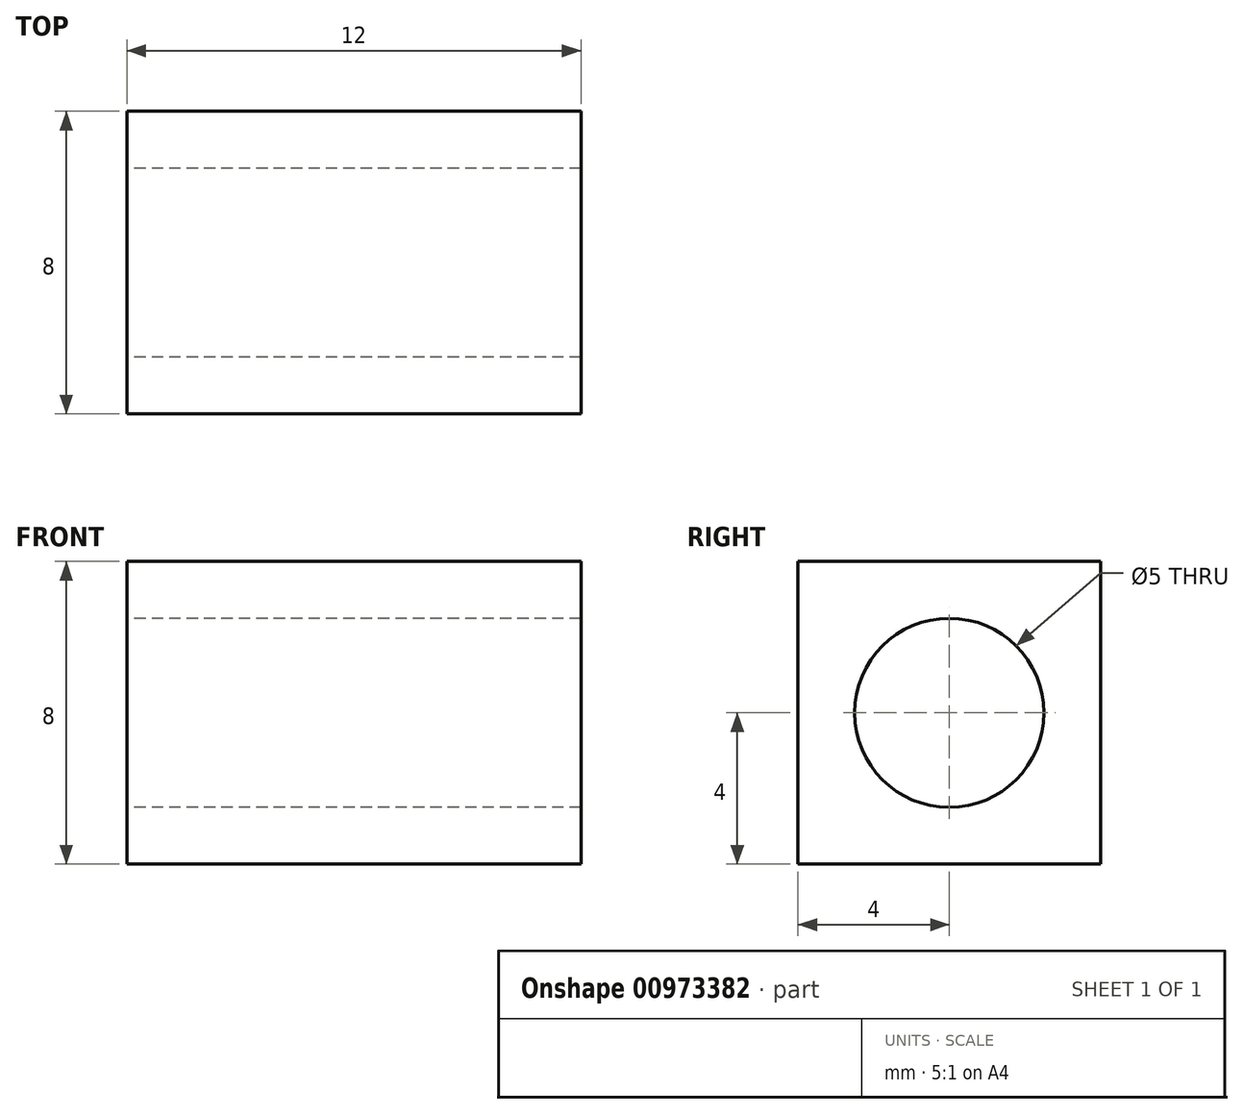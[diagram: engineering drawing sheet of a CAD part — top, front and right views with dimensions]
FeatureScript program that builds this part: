
annotation { "Feature Type Name" : "Feature", "Feature Type Description" : "" }
export const myFeature = defineFeature(function(context is Context, id is Id, definition is map)
    precondition{}
    {
        {
            var Q0;
            Q0=qCreatedBy(makeId("Right.planeOp"),FACE);
            var sketch = newSketch(context, id + "F0", { "sketchPlane" : qUnion([Q0])});
            skLineSegment(sketch, "E0.bottom", {"start": v(0, 0) * mm, "end": v(-8, 0) * mm});
            skLineSegment(sketch, "E0.top", {"start": v(0, 8) * mm, "end": v(-8, 8) * mm});
            skLineSegment(sketch, "E0.left", {"start": v(0, 0) * mm, "end": v(0, 8) * mm});
            skLineSegment(sketch, "E0.right", {"start": v(-8, 0) * mm, "end": v(-8, 8) * mm});
            skCircle(sketch, "E1", {"center": v(-4, 4) * mm, "radius": 2.5 * mm});
            skPoint(sketch, "E1.centerSnap0", {"position": v(0, 4) * mm});
            skPoint(sketch, "E1.centerSnap1", {"position": v(-4, 8) * mm});
            skSolve(sketch);
        }
        {
            var Q0;
            Q0=makeQuery(id+"F0.imprint","IMPRINT",FACE,{"disambiguationData":[TD([[makeQuery(id+"F0.imprint","IMPRINT",EDGE,{"derivedFrom":sQuery(id+"F0.wireOp",EDGE,"E0.bottom")}),-1.0]])]});
            extrude(context, id + "F1", {"entities" : qUnion([Q0]), "depth" : 12 * mm, "offsetDistance" : 25 * mm});
        }
    });
